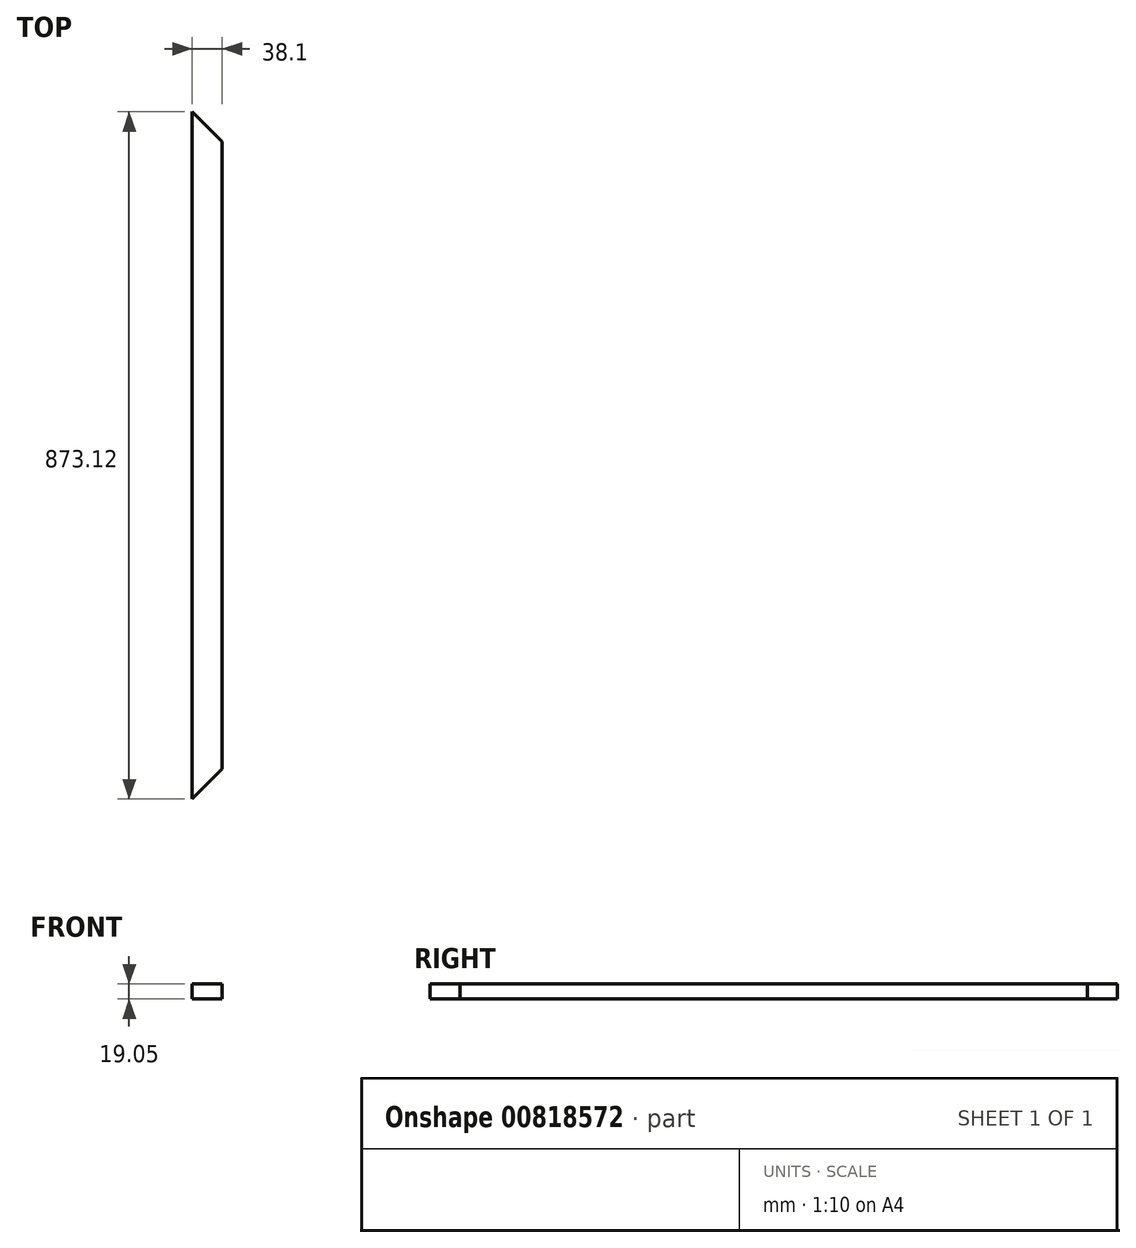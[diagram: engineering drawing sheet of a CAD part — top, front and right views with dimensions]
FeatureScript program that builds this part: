
annotation { "Feature Type Name" : "Feature", "Feature Type Description" : "" }
export const myFeature = defineFeature(function(context is Context, id is Id, definition is map)
    precondition{}
    {
        {
            var Q0;
            Q0=qCreatedBy(makeId("Front.planeOp"),FACE);
            var sketch = newSketch(context, id + "F0", { "sketchPlane" : qUnion([Q0])});
            skLineSegment(sketch, "E0.bottom", {"start": v(-12.82, 8.22) * mm, "end": v(25.28, 8.22) * mm});
            skLineSegment(sketch, "E0.top", {"start": v(-12.82, -10.83) * mm, "end": v(25.28, -10.83) * mm});
            skLineSegment(sketch, "E0.left", {"start": v(-12.82, 8.22) * mm, "end": v(-12.82, -10.83) * mm});
            skLineSegment(sketch, "E0.right", {"start": v(25.28, 8.22) * mm, "end": v(25.28, -10.83) * mm});
            skSolve(sketch);
        }
        {
            var Q0;
            Q0 = qSketchRegion(id + "F0", true);
            extrude(context, id + "F1", {"entities" : qUnion([Q0]), "depth" : 873.12 * mm, "offsetDistance" : 25.4 * mm});
        }
        {
            var Q0;
            Q0=makeQuery(id+"F1.opExtrude","SWEPT_FACE",FACE,{"disambiguationData":[OSD([sQuery(id+"F0.wireOp",EDGE,"E0.bottom")])]});
            var sketch = newSketch(context, id + "F2", { "sketchPlane" : qUnion([Q0])});
            skLineSegment(sketch, "E1", {"start": v(-12.82, -873.12) * mm, "end": v(25.28, -835.02) * mm});
            skLineSegment(sketch, "E2", {"start": v(25.28, -835.02) * mm, "end": v(25.28, -873.12) * mm});
            skLineSegment(sketch, "E3", {"start": v(25.28, -873.12) * mm, "end": v(-12.82, -873.12) * mm});
            skLineSegment(sketch, "E4", {"start": v(25.28, 0) * mm, "end": v(25.28, -38.1) * mm});
            skLineSegment(sketch, "E5", {"start": v(25.28, -38.1) * mm, "end": v(-12.82, 0) * mm});
            skLineSegment(sketch, "E6", {"start": v(-12.82, 0) * mm, "end": v(25.28, 0) * mm});
            skSolve(sketch);
        }
        {
            var Q0;
            Q0 = qSketchRegion(id + "F2", true);
            extrude(context, id + "F3", {"entities" : qUnion([Q0]), "operationType" : NewBodyOperationType.REMOVE, "oppositeDirection" : true, "depth" : 25.4 * mm, "offsetDistance" : 25.4 * mm});
        }
    });
